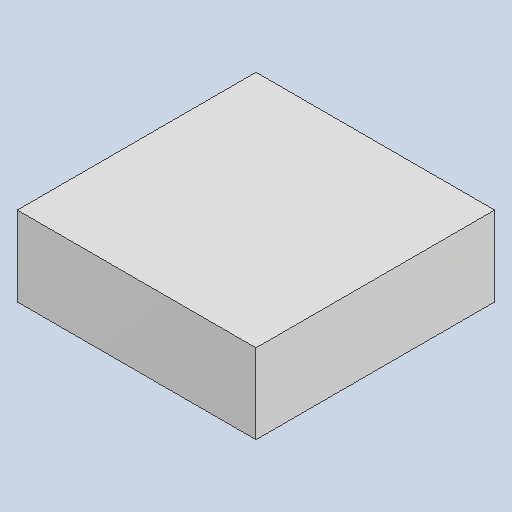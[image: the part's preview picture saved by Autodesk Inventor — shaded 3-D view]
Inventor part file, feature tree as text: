
AUTODESK INVENTOR PART (.ipt)
format: ipt  version: 2023.4 (Build 274418000, 418)  size: 79,872 bytes
history: native  units: mm
features: extrude x1
ambient origin geometry x8: Origin, YZ Plane, XZ Plane, XY Plane, X Axis, Y Axis, Z Axis, Center Point
bodies: Solid1 (feature_tree)
feature tree (1):
  extrude  "Extruded_15"  [1 undecoded]
note: 1 required parameter value undecoded (feature->parameter linkage not recoverable at this tier; creation-order binding heuristic only, values carry confidence <= 0.55)
